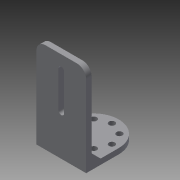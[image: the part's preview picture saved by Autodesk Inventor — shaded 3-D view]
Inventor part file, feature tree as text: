
AUTODESK INVENTOR PART (.ipt)
format: ipt  version: 2013 (Build 170138000, 138)  size: 143,360 bytes
history: native  units: mm
features: extrude x4, sketch x3, hole x1, mirror x1, chamfer x1, fillet x1
ambient origin geometry x8: Origin, YZ Plane, XZ Plane, XY Plane, X Axis, Y Axis, Z Axis, Center Point
bodies: Solid1 (feature_tree)
feature tree (11):
  sketch  "Sketch1"  dims[d0=55.0mm d1=36.0mm]
  extrude  "Extrusion1"  Depth=36.0mm
  extrude  "Extrusion2"  Depth=6.0mm TaperAngle=0.0deg
  sketch  "Sketch2"  dims[d2=6.0mm d3=6.0mm d4=0.0mm]
  hole  "Hole1"  [1 undecoded]
  extrude  "Extrusion3"  Depth=20.0mm
  mirror  "Mirror3"
  chamfer  "Chamfer1"  Distance=80.0mm Angle=360.0deg
  extrude  "Extrusion4"  Depth=6.0mm
  fillet  "Fillet1"  Radius=10.0mm
  sketch  "Sketch3"  dims[d5=100.0mm d6=0.0mm d7=20.0mm d8=20.0mm d9=80.0mm d11=360.0deg d13=6.6mm d14=6.0mm d15=12.6mm d16=2.0mm d17=90.0deg d18=8.0mm d19=20.594885mm d20=6.0mm d21=10.0mm d22=10.0mm d23=0.0mm d24=10.0mm d25=2.0mm d26=45.0deg d27=15.0mm d28=40.0mm d29=3.15mm d30=3.15mm d31=10.0mm d32=0.0mm d33=10.0mm]
note: 1 required parameter value undecoded (feature->parameter linkage not recoverable at this tier; creation-order binding heuristic only, values carry confidence <= 0.55)
